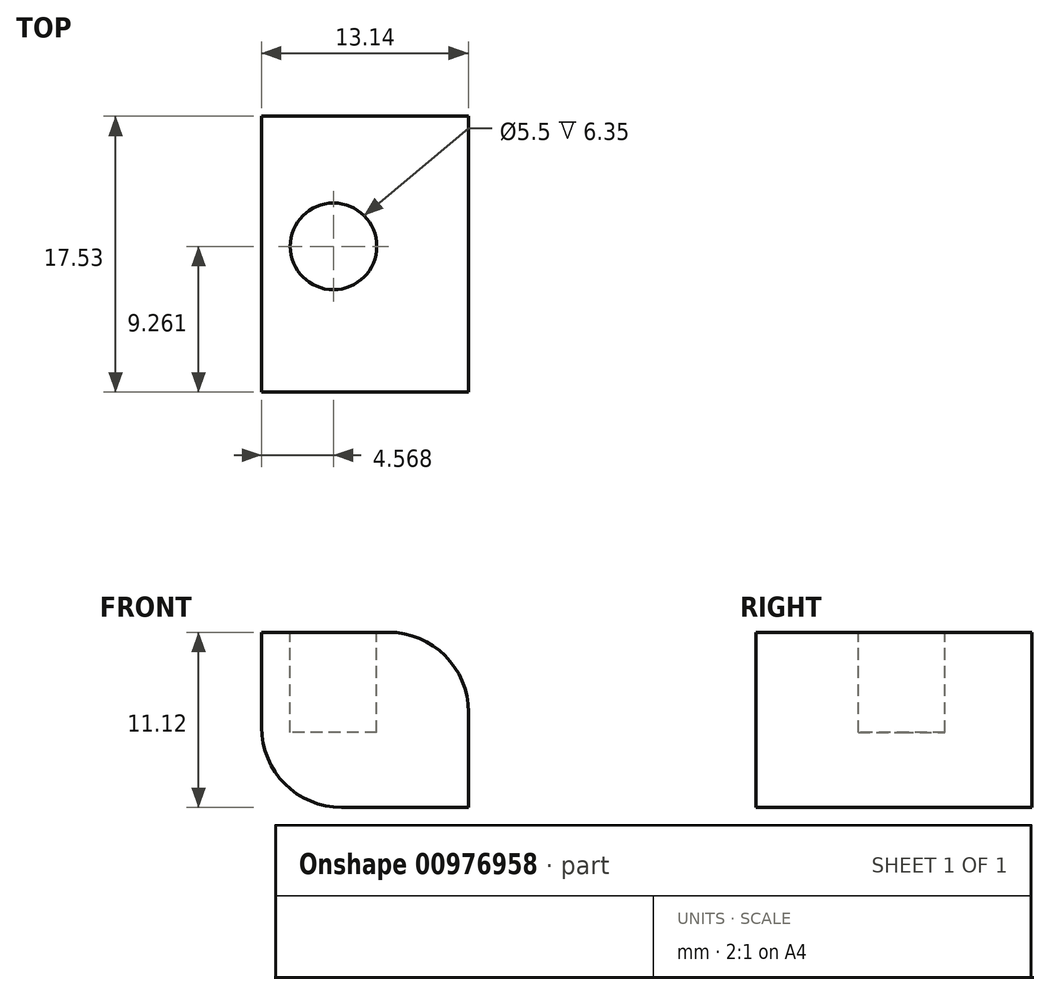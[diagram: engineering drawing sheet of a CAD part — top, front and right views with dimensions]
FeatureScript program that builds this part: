
annotation { "Feature Type Name" : "Feature", "Feature Type Description" : "" }
export const myFeature = defineFeature(function(context is Context, id is Id, definition is map)
    precondition{}
    {
        {
            var Q0;
            Q0=qCreatedBy(makeId("Front.planeOp"),FACE);
            var sketch = newSketch(context, id + "F0", { "sketchPlane" : qUnion([Q0])});
            skLineSegment(sketch, "E0.bottom", {"start": v(-41.6, 37.36) * mm, "end": v(-28.45, 37.36) * mm});
            skLineSegment(sketch, "E0.top", {"start": v(-41.6, 26.24) * mm, "end": v(-28.45, 26.24) * mm});
            skLineSegment(sketch, "E0.left", {"start": v(-41.6, 37.36) * mm, "end": v(-41.6, 26.24) * mm});
            skLineSegment(sketch, "E0.right", {"start": v(-28.45, 37.36) * mm, "end": v(-28.45, 26.24) * mm});
            skSolve(sketch);
        }
        {
            var Q0;
            Q0=makeQuery(id+"F0.imprint","IMPRINT",FACE,{"disambiguationData":[TD([[makeQuery(id+"F0.imprint","IMPRINT",EDGE,{"derivedFrom":sQuery(id+"F0.wireOp",EDGE,"E0.bottom")}),-1.0]])]});
            extrude(context, id + "F1", {"entities" : qUnion([Q0]), "depth" : 17.53 * mm, "offsetDistance" : 25.4 * mm});
        }
        {
            var Q0;
            Q0=makeQuery(id+"F1.opExtrude","SWEPT_FACE",FACE,{"disambiguationData":[OSD([sQuery(id+"F0.wireOp",EDGE,"E0.bottom")])]});
            var sketch = newSketch(context, id + "F2", { "sketchPlane" : qUnion([Q0])});
            skCircle(sketch, "E1", {"center": v(-37.02, -8.27) * mm, "radius": 2.75 * mm});
            skSolve(sketch);
        }
        {
            var Q0;
            Q0=makeQuery(id+"F2.imprint","IMPRINT",FACE,{"disambiguationData":[TD([[makeQuery(id+"F2.imprint","IMPRINT",EDGE,{"derivedFrom":sQuery(id+"F2.wireOp",EDGE,"E1")}),1.0]])]});
            extrude(context, id + "F3", {"entities" : qUnion([Q0]), "operationType" : NewBodyOperationType.REMOVE, "oppositeDirection" : true, "depth" : 6.35 * mm, "offsetDistance" : 25.4 * mm});
        }
        {
            var Q0;
            Q0=makeQuery(id+"F1.opExtrude","SWEPT_EDGE",EDGE,{"disambiguationData":[OSD([sQuery(id+"F0.wireOp",EDGE,"E0.bottom"),sQuery(id+"F0.wireOp",EDGE,"E0.right")])]});
            var Q1;
            Q1=makeQuery(id+"F1.opExtrude","SWEPT_EDGE",EDGE,{"disambiguationData":[OSD([sQuery(id+"F0.wireOp",EDGE,"E0.top"),sQuery(id+"F0.wireOp",EDGE,"E0.left")])]});
            fillet(context, id + "F4", {"entities" : qUnion([Q0, Q1]), "radius" : 5.08 * mm, "tangentPropagation" : true, "allowEdgeOverflow" : false});
        }
    });
